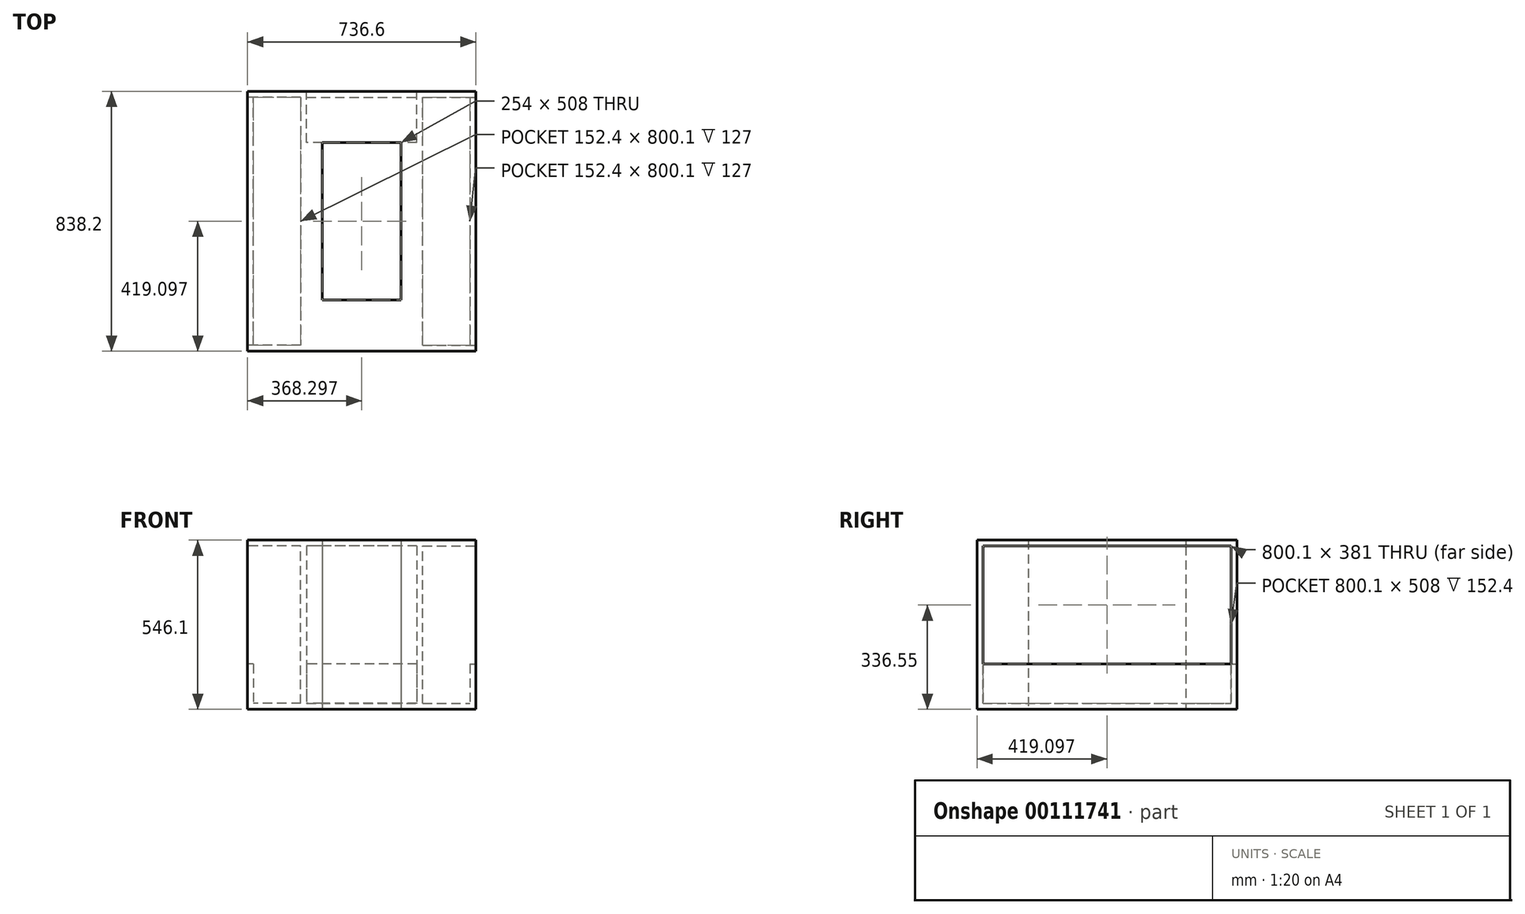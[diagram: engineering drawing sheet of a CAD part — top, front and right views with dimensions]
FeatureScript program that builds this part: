
annotation { "Feature Type Name" : "Feature", "Feature Type Description" : "" }
export const myFeature = defineFeature(function(context is Context, id is Id, definition is map)
    precondition{}
    {
        {
            var Q0;
            Q0=qCreatedBy(makeId("Top.planeOp"),FACE);
            var sketch = newSketch(context, id + "F0", { "sketchPlane" : qUnion([Q0])});
            skLineSegment(sketch, "E0.bottom", {"start": v(-81.86, -146.54) * mm, "end": v(654.74, -146.54) * mm});
            skLineSegment(sketch, "E0.top", {"start": v(-81.86, 691.66) * mm, "end": v(654.74, 691.66) * mm});
            skLineSegment(sketch, "E0.left", {"start": v(-81.86, -146.54) * mm, "end": v(-81.86, 691.66) * mm});
            skLineSegment(sketch, "E0.right", {"start": v(654.74, -146.54) * mm, "end": v(654.74, 691.66) * mm});
            skLineSegment(sketch, "E1.bottom", {"start": v(159.44, 18.56) * mm, "end": v(413.44, 18.56) * mm});
            skLineSegment(sketch, "E1.top", {"start": v(159.44, 526.56) * mm, "end": v(413.44, 526.56) * mm});
            skLineSegment(sketch, "E1.left", {"start": v(159.44, 18.56) * mm, "end": v(159.44, 526.56) * mm});
            skLineSegment(sketch, "E1.right", {"start": v(413.44, 18.56) * mm, "end": v(413.44, 526.56) * mm});
            skSolve(sketch);
        }
        {
            var Q0;
            Q0=makeQuery(id+"F0.imprint","IMPRINT",FACE,{"disambiguationData":[TD([[makeQuery(id+"F0.imprint","IMPRINT",EDGE,{"derivedFrom":sQuery(id+"F0.wireOp",EDGE,"E0.bottom")}),1.0]])]});
            extrude(context, id + "F1", {"entities" : qUnion([Q0]), "depth" : 546.1 * mm});
        }
        {
            var Q0;
            Q0=makeQuery(id+"F1.opExtrude","SWEPT_FACE",FACE,{"disambiguationData":[OSD([sQuery(id+"F0.wireOp",EDGE,"E0.right")])]});
            var sketch = newSketch(context, id + "F2", { "sketchPlane" : qUnion([Q0])});
            skLineSegment(sketch, "E2.bottom", {"start": v(-127.5, 19.05) * mm, "end": v(672.6, 19.05) * mm});
            skLineSegment(sketch, "E2.top", {"start": v(-127.5, 527.05) * mm, "end": v(672.6, 527.05) * mm});
            skLineSegment(sketch, "E2.left", {"start": v(-127.5, 19.05) * mm, "end": v(-127.5, 527.05) * mm});
            skLineSegment(sketch, "E2.right", {"start": v(672.6, 19.05) * mm, "end": v(672.6, 527.05) * mm});
            skSolve(sketch);
        }
        {
            var Q0;
            Q0=makeQuery(id+"F2.imprint","IMPRINT",FACE,{"disambiguationData":[TD([[makeQuery(id+"F2.imprint","IMPRINT",EDGE,{"derivedFrom":sQuery(id+"F2.wireOp",EDGE,"E2.bottom")}),1.0]])]});
            extrude(context, id + "F3", {"entities" : qUnion([Q0]), "operationType" : NewBodyOperationType.REMOVE, "oppositeDirection" : true, "depth" : 171.45 * mm});
        }
        {
            var Q0;
            Q0=makeQuery(id+"F1.opExtrude","SWEPT_FACE",FACE,{"disambiguationData":[OSD([sQuery(id+"F0.wireOp",EDGE,"E0.left")])]});
            var sketch = newSketch(context, id + "F4", { "sketchPlane" : qUnion([Q0])});
            skLineSegment(sketch, "E3.bottom", {"start": v(-672.6, 19.05) * mm, "end": v(127.5, 19.05) * mm});
            skLineSegment(sketch, "E3.top", {"start": v(-672.6, 527.05) * mm, "end": v(127.5, 527.05) * mm});
            skLineSegment(sketch, "E3.left", {"start": v(-672.6, 19.05) * mm, "end": v(-672.6, 527.05) * mm});
            skLineSegment(sketch, "E3.right", {"start": v(127.5, 19.05) * mm, "end": v(127.5, 527.05) * mm});
            skSolve(sketch);
        }
        {
            var Q0;
            Q0=makeQuery(id+"F4.imprint","IMPRINT",FACE,{"disambiguationData":[TD([[makeQuery(id+"F4.imprint","IMPRINT",EDGE,{"derivedFrom":sQuery(id+"F4.wireOp",EDGE,"E3.bottom")}),1.0]])]});
            extrude(context, id + "F5", {"entities" : qUnion([Q0]), "operationType" : NewBodyOperationType.REMOVE, "oppositeDirection" : true, "depth" : 171.45 * mm});
        }
        {
            var Q0;
            Q0=makeQuery(id+"F3.boolean.opBoolean","COPY",FACE,{"derivedFrom":makeQuery(id+"F3.opExtrude","SWEPT_FACE",FACE,{"disambiguationData":[OSD([sQuery(id+"F2.wireOp",EDGE,"E2.bottom")])]})});
            var sketch = newSketch(context, id + "F6", { "sketchPlane" : qUnion([Q0])});
            skLineSegment(sketch, "E4.bottom", {"start": v(654.74, 672.6) * mm, "end": v(635.69, 672.6) * mm});
            skLineSegment(sketch, "E4.top", {"start": v(654.74, -127.5) * mm, "end": v(635.69, -127.5) * mm});
            skLineSegment(sketch, "E4.left", {"start": v(654.74, 672.6) * mm, "end": v(654.74, -127.5) * mm});
            skLineSegment(sketch, "E4.right", {"start": v(635.69, 672.6) * mm, "end": v(635.69, -127.5) * mm});
            skSolve(sketch);
        }
        {
            var Q0;
            Q0=makeQuery(id+"F6.imprint","IMPRINT",FACE,{"disambiguationData":[TD([[makeQuery(id+"F6.imprint","IMPRINT",EDGE,{"derivedFrom":sQuery(id+"F6.wireOp",EDGE,"E4.bottom")}),-1.0]])]});
            extrude(context, id + "F7", {"entities" : qUnion([Q0]), "operationType" : NewBodyOperationType.ADD, "depth" : 127 * mm});
        }
        {
            var Q0;
            Q0=makeQuery(id+"F5.boolean.opBoolean","COPY",FACE,{"derivedFrom":makeQuery(id+"F5.opExtrude","SWEPT_FACE",FACE,{"disambiguationData":[OSD([sQuery(id+"F4.wireOp",EDGE,"E3.bottom")])]})});
            var sketch = newSketch(context, id + "F8", { "sketchPlane" : qUnion([Q0])});
            skLineSegment(sketch, "E5.bottom", {"start": v(-62.81, -127.5) * mm, "end": v(-81.86, -127.5) * mm});
            skLineSegment(sketch, "E5.top", {"start": v(-62.81, 672.6) * mm, "end": v(-81.86, 672.6) * mm});
            skLineSegment(sketch, "E5.left", {"start": v(-62.81, -127.5) * mm, "end": v(-62.81, 672.6) * mm});
            skLineSegment(sketch, "E5.right", {"start": v(-81.86, -127.5) * mm, "end": v(-81.86, 672.6) * mm});
            skSolve(sketch);
        }
        {
            var Q0;
            Q0=makeQuery(id+"F8.imprint","IMPRINT",FACE,{"disambiguationData":[TD([[makeQuery(id+"F8.imprint","IMPRINT",EDGE,{"derivedFrom":sQuery(id+"F8.wireOp",EDGE,"E5.bottom")}),-1.0]])]});
            extrude(context, id + "F9", {"entities" : qUnion([Q0]), "operationType" : NewBodyOperationType.ADD, "depth" : 127 * mm});
        }
        {
            var Q0;
            Q0=makeQuery(id+"F1.opExtrude","SWEPT_FACE",FACE,{"disambiguationData":[OSD([sQuery(id+"F0.wireOp",EDGE,"E0.top")])]});
            var sketch = newSketch(context, id + "F10", { "sketchPlane" : qUnion([Q0])});
            skLineSegment(sketch, "E6.bottom", {"start": v(-464.24, 527.05) * mm, "end": v(-108.64, 527.05) * mm});
            skLineSegment(sketch, "E6.top", {"start": v(-464.24, 19.05) * mm, "end": v(-108.64, 19.05) * mm});
            skLineSegment(sketch, "E6.left", {"start": v(-464.24, 527.05) * mm, "end": v(-464.24, 19.05) * mm});
            skLineSegment(sketch, "E6.right", {"start": v(-108.64, 527.05) * mm, "end": v(-108.64, 19.05) * mm});
            skSolve(sketch);
        }
        {
            var Q0;
            Q0=makeQuery(id+"F10.imprint","IMPRINT",FACE,{"disambiguationData":[TD([[makeQuery(id+"F10.imprint","IMPRINT",EDGE,{"derivedFrom":sQuery(id+"F10.wireOp",EDGE,"E6.bottom")}),-1.0]])]});
            extrude(context, id + "F11", {"entities" : qUnion([Q0]), "operationType" : NewBodyOperationType.REMOVE, "oppositeDirection" : true, "depth" : 165.1 * mm});
        }
        {
            var Q0;
            Q0=makeQuery(id+"F11.boolean.opBoolean","COPY",FACE,{"derivedFrom":makeQuery(id+"F11.opExtrude","SWEPT_FACE",FACE,{"disambiguationData":[OSD([sQuery(id+"F10.wireOp",EDGE,"E6.top")])]})});
            var sketch = newSketch(context, id + "F12", { "sketchPlane" : qUnion([Q0])});
            skLineSegment(sketch, "E7.bottom", {"start": v(108.64, 691.66) * mm, "end": v(464.24, 691.66) * mm});
            skLineSegment(sketch, "E7.top", {"start": v(108.64, 672.6) * mm, "end": v(464.24, 672.6) * mm});
            skLineSegment(sketch, "E7.left", {"start": v(108.64, 691.66) * mm, "end": v(108.64, 672.6) * mm});
            skLineSegment(sketch, "E7.right", {"start": v(464.24, 691.66) * mm, "end": v(464.24, 672.6) * mm});
            skSolve(sketch);
        }
        {
            var Q0;
            Q0=makeQuery(id+"F12.imprint","IMPRINT",FACE,{"disambiguationData":[TD([[makeQuery(id+"F12.imprint","IMPRINT",EDGE,{"derivedFrom":sQuery(id+"F12.wireOp",EDGE,"E7.bottom")}),1.0]])]});
            extrude(context, id + "F13", {"entities" : qUnion([Q0]), "operationType" : NewBodyOperationType.ADD, "depth" : 127 * mm});
        }
    });
